# Revit family: Sanitary_Showers_DURAVIT-AG_Hand-shower-240x120x63-mm-UV0650017
name_source: partatom
category: Plumbing Fixtures
revit_build: Autodesk Revit 2018 (Build: 20180329_1100(x64)
units: mm (PartAtom-declared; Revit-internal decimal feet)

## family parameters
Always vertical = No
Cut with Voids When Loaded = No
OmniClass Number = 23.31.17.00
OmniClass Title = Showers
Part Type = Normal
Room Calculation Point = No
Round Connector Dimension = Use Diameter
Shared = No
Work Plane-Based = Yes

## types (2) — shared parameters
BIMobject category = Showers
Default Elevation = 1219.2 mm  [stored 4 ft]
Design country = Germany
ETIM classification = EC010161 | Hand shower
Edition number = 1
IFC Classification = Sanitary Terminal
Installation instructions = https://pro.duravit.com
Manufacturer = Duravit
Manufacturer country = Germany
Manufacturer name = DURAVIT AG
Masterformat 2014 Code = 22 41 23
Masterformat 2014 Description = Residential Showers
Material main = Plastic
Model = Hand shower 240x120x63 mm - UV0650017
OmniClass Code = 23-31 17 00
OmniClass Description = Showers
Product Guid = 7fcec869-f390-43c2-bfd0-9a31852d595f
Product SKU = Hand-shower-240x120x63-mm-UV0650017
Product certification = https://pro.duravit.com
Product data url = https://bimobject.com
Product family = Universal
Product group = Hand shower
Product name = Hand shower 240x120x63 mm - UV0650017
Product url = https://pro.duravit.com
QR code = https://bimobject.com
Technical description = https://pro.duravit.com
UNSPSC Code = 30181503
URL = https://www.duravit.com
Uniclass 2015 Code = SL_35_80_80
Uniclass 2015 Name = Showers
Uniformat II Code = D2010
Uniformat II Description = Plumbing Fixtures
Weight Net (Kg) = 0.14
Youtube clip = https://pro.duravit.com

## per-type parameters (varying)
| type | Description | Details material | Main material | Secondary material |
| 10 - Chrome | Duravit Hand shower Chrome High Gloss 240x120x63 mm - UV0650017010 | Duravit - Plastic - Dark Grey Plastic | Duravit - Metal - 10 - Chrome | Duravit - Plastic - White Plastic |
| 46 - Black Matt | Duravit Hand shower Black Matt 240x120x63 mm - UV0650017046 | Duravit - Metal - 46 - Black Matt | Duravit - Metal - 46 - Black Matt | Duravit - Metal - 46 - Black Matt |

note: [stored X ft] marks values corroborated as IEEE doubles in the binary element streams (Revit-internal decimal feet)

## geometry (parser evidence)
native form markers: Sweep x3
no freeform markers — native parametric forms only
